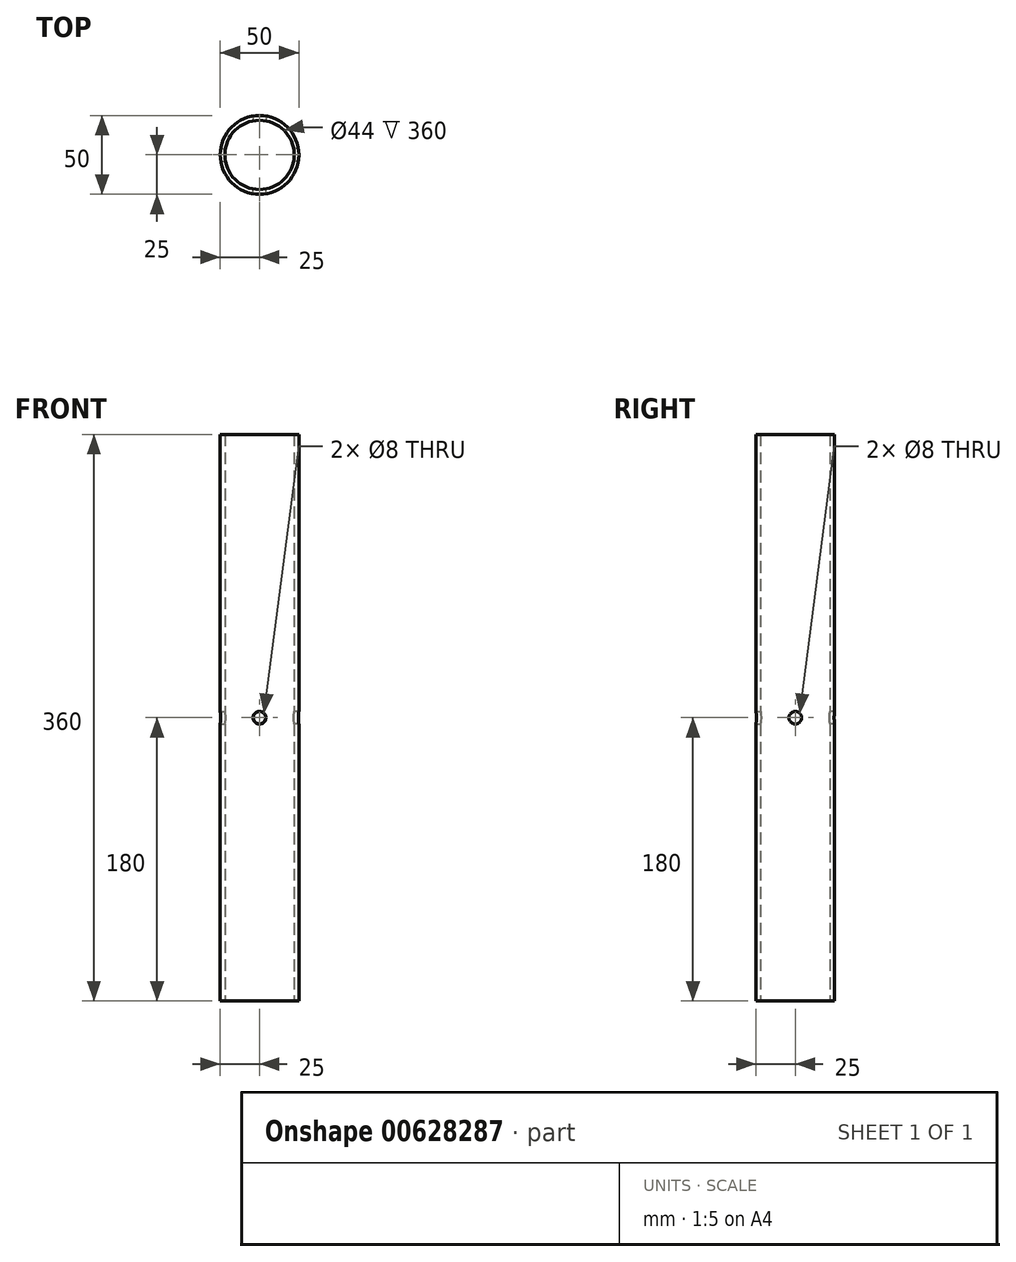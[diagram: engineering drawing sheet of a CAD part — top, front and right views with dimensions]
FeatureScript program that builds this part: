
annotation { "Feature Type Name" : "Feature", "Feature Type Description" : "" }
export const myFeature = defineFeature(function(context is Context, id is Id, definition is map)
    precondition{}
    {
        {
            var Q0;
            Q0=qCreatedBy(makeId("Top.planeOp"),FACE);
            var sketch = newSketch(context, id + "F0", { "sketchPlane" : qUnion([Q0])});
            skCircle(sketch, "E0", {"center": v(0, 0) * mm, "radius": 25 * mm});
            skCircle(sketch, "E1", {"center": v(0, 0) * mm, "radius": 22 * mm});
            skCircle(sketch, "E2.cCircle", {"center": v(0, 0) * mm, "radius": 22 * mm, "construction": true});
            skPoint(sketch, "E2.0.midPoint", {"position": v(13.5, -17.37) * mm});
            skSolve(sketch);
        }
        {
            var Q0;
            Q0=makeQuery(id+"F0.imprint","IMPRINT",FACE,{"disambiguationData":[TD([[makeQuery(id+"F0.imprint","IMPRINT",EDGE,{"derivedFrom":sQuery(id+"F0.wireOp",EDGE,"E0")}),1.0]])]});
            var Q1;
            {var subQ0=sQuery(id+"F0.wireOp",EDGE,"E2.2");var subQ1=sQuery(id+"F0.wireOp",EDGE,"E0");var subQ2=makeQuery(id+"F0.imprint","INTERSECT",VERTEX,{"disambiguationData":[OD(1.0)],"derivedFrom":[subQ1,subQ0]});Q1=makeQuery(id+"F0.imprint","IMPRINT",FACE,{"disambiguationData":[TD([[makeQuery(id+"F0.imprint","IMPRINT",EDGE,{"disambiguationData":[TD([[subQ2,-1.0]])],"derivedFrom":subQ1}),1.0]])]});}
            var Q2;
            {var subQ0=sQuery(id+"F0.wireOp",EDGE,"E2.3");var subQ1=sQuery(id+"F0.wireOp",EDGE,"E0");var subQ2=makeQuery(id+"F0.imprint","INTERSECT",VERTEX,{"disambiguationData":[OD(1.0)],"derivedFrom":[subQ1,subQ0]});Q2=makeQuery(id+"F0.imprint","IMPRINT",FACE,{"disambiguationData":[TD([[makeQuery(id+"F0.imprint","IMPRINT",EDGE,{"disambiguationData":[TD([[subQ2,1.0]])],"derivedFrom":subQ1}),1.0]])]});}
            var Q3;
            {var subQ0=sQuery(id+"F0.wireOp",EDGE,"E2.1");var subQ1=sQuery(id+"F0.wireOp",EDGE,"E0");var subQ2=makeQuery(id+"F0.imprint","INTERSECT",VERTEX,{"disambiguationData":[OD(1.0)],"derivedFrom":[subQ1,subQ0]});Q3=makeQuery(id+"F0.imprint","IMPRINT",FACE,{"disambiguationData":[TD([[makeQuery(id+"F0.imprint","IMPRINT",EDGE,{"disambiguationData":[TD([[subQ2,-1.0]])],"derivedFrom":subQ1}),1.0]])]});}
            var Q4;
            {var subQ0=sQuery(id+"F0.wireOp",EDGE,"E2.3");var subQ1=sQuery(id+"F0.wireOp",EDGE,"E0");var subQ2=makeQuery(id+"F0.imprint","INTERSECT",VERTEX,{"disambiguationData":[OD(0.0)],"derivedFrom":[subQ1,subQ0]});Q4=makeQuery(id+"F0.imprint","IMPRINT",FACE,{"disambiguationData":[TD([[makeQuery(id+"F0.imprint","IMPRINT",EDGE,{"disambiguationData":[TD([[subQ2,-1.0]])],"derivedFrom":subQ1}),1.0]])]});}
            extrude(context, id + "F1", {"entities" : qUnion([Q0, Q1, Q2, Q3, Q4]), "depth" : 90 * mm, "offsetDistance" : 25 * mm});
        }
        {
            var Q0;
            Q0=makeQuery(id+"F1.opExtrude","CAP_FACE",FACE,{"disambiguationData":[OSD([sQuery(id+"F0.wireOp",EDGE,"E0"),sQuery(id+"F0.wireOp",EDGE,"E1")])],"isStart":false});
            extrude(context, id + "F2", {"entities" : qUnion([Q0]), "operationType" : NewBodyOperationType.ADD, "depth" : 90 * mm, "offsetDistance" : 25 * mm});
        }
        {
            var Q0;
            Q0=qCreatedBy(makeId("Right.planeOp"),FACE);
            var sketch = newSketch(context, id + "F3", { "sketchPlane" : qUnion([Q0])});
            skCircle(sketch, "E3", {"center": v(0, 0) * mm, "radius": 4 * mm});
            skSolve(sketch);
        }
        {
            var Q0;
            Q0 = qSketchRegion(id + "F3", true);
            extrude(context, id + "F4", {"entities" : qUnion([Q0]), "operationType" : NewBodyOperationType.REMOVE, "depth" : 25 * mm, "offsetDistance" : 25 * mm});
        }
        {
            var Q0;
            Q0=makeQuery(id+"F3.imprint","IMPRINT",FACE,{"disambiguationData":[TD([[makeQuery(id+"F3.imprint","IMPRINT",EDGE,{"derivedFrom":sQuery(id+"F3.wireOp",EDGE,"E3")}),1.0]])]});
            extrude(context, id + "F5", {"entities" : qUnion([Q0]), "operationType" : NewBodyOperationType.REMOVE, "oppositeDirection" : true, "depth" : 25 * mm, "offsetDistance" : 25 * mm});
        }
        {
            var Q0;
            Q0=qCreatedBy(makeId("Front.planeOp"),FACE);
            var sketch = newSketch(context, id + "F6", { "sketchPlane" : qUnion([Q0])});
            skCircle(sketch, "E4", {"center": v(0, 0) * mm, "radius": 4 * mm});
            skSolve(sketch);
        }
        {
            var Q0;
            Q0=makeQuery(id+"F6.imprint","IMPRINT",FACE,{"disambiguationData":[TD([[makeQuery(id+"F6.imprint","IMPRINT",EDGE,{"derivedFrom":sQuery(id+"F6.wireOp",EDGE,"E4")}),1.0]])]});
            extrude(context, id + "F7", {"entities" : qUnion([Q0]), "operationType" : NewBodyOperationType.REMOVE, "depth" : 25 * mm, "offsetDistance" : 25 * mm});
        }
        {
            var Q0;
            Q0 = qSketchRegion(id + "F6", true);
            extrude(context, id + "F8", {"entities" : qUnion([Q0]), "operationType" : NewBodyOperationType.REMOVE, "oppositeDirection" : true, "depth" : 25 * mm, "offsetDistance" : 25 * mm});
        }
        {
            var Q0;
            Q0=makeQuery(id+"F1.opExtrude","SWEPT_BODY",BODY,{"disambiguationData":[OSD([sQuery(id+"F0.wireOp",EDGE,"E0"),sQuery(id+"F0.wireOp",EDGE,"E1")])]});
            var Q1;
            Q1=qCreatedBy(makeId("Top.planeOp"),FACE);
            mirror(context, id + "F9", {"operationType" : NewBodyOperationType.ADD, "entities" : qUnion([Q0]), "mirrorPlane" : qUnion([Q1])});
        }
    });
